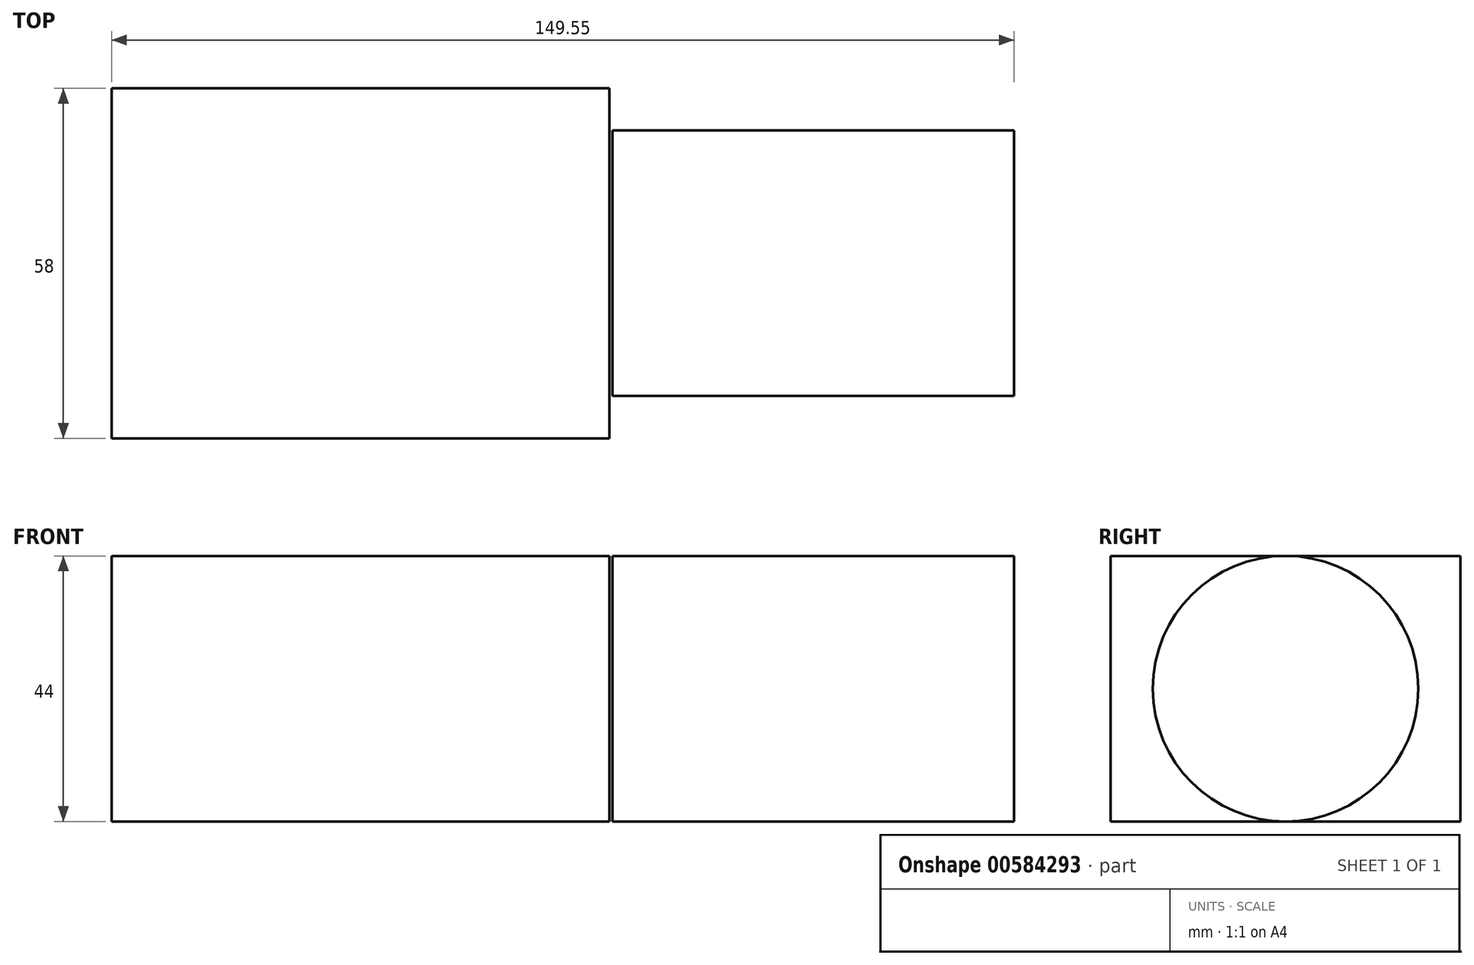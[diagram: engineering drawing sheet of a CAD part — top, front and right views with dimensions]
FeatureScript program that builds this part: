
annotation { "Feature Type Name" : "Feature", "Feature Type Description" : "" }
export const myFeature = defineFeature(function(context is Context, id is Id, definition is map)
    precondition{}
    {
        {
            var Q0;
            Q0=qCreatedBy(makeId("Front.planeOp"),FACE);
            var sketch = newSketch(context, id + "F0", { "sketchPlane" : qUnion([Q0])});
            skLineSegment(sketch, "E0.bottom", {"start": v(41.25, 22) * mm, "end": v(-41.25, 22) * mm});
            skLineSegment(sketch, "E0.top", {"start": v(41.25, -22) * mm, "end": v(-41.25, -22) * mm});
            skLineSegment(sketch, "E0.left", {"start": v(41.25, 22) * mm, "end": v(41.25, -22) * mm});
            skLineSegment(sketch, "E0.right", {"start": v(-41.25, 22) * mm, "end": v(-41.25, -22) * mm});
            skPoint(sketch, "E0.middle", {"position": v(0, 0) * mm});
            skLineSegment(sketch, "E1", {"start": v(41.25, 0) * mm, "end": v(107.78, 0) * mm});
            skPoint(sketch, "E1.endSnap0", {"position": v(41.25, 0) * mm});
            skSolve(sketch);
        }
        {
            var Q0;
            Q0=qCreatedBy(makeId("Front.planeOp"),FACE);
            var sketch = newSketch(context, id + "F1", { "sketchPlane" : qUnion([Q0])});
            skLineSegment(sketch, "E2.bottom", {"start": v(41.77, 0) * mm, "end": v(108.3, 0) * mm});
            skLineSegment(sketch, "E2.top", {"start": v(41.77, 22) * mm, "end": v(108.3, 22) * mm});
            skLineSegment(sketch, "E2.left", {"start": v(41.77, 0) * mm, "end": v(41.77, 22) * mm});
            skLineSegment(sketch, "E2.right", {"start": v(108.3, 0) * mm, "end": v(108.3, 22) * mm});
            skSolve(sketch);
        }
        {
            var Q0;
            Q0=makeQuery(id+"F1.imprint","IMPRINT",FACE,{"disambiguationData":[TD([[makeQuery(id+"F1.imprint","IMPRINT",EDGE,{"derivedFrom":sQuery(id+"F1.wireOp",EDGE,"E2.bottom")}),1.0]])]});
            var Q1;
            Q1=sQuery(id+"F1.wireOp",EDGE,"E2.bottom");
            revolve(context, id + "F2", {"entities" : qUnion([Q0]), "axis" : qUnion([Q1]), "revolveType" : RevolveType.FULL});
        }
        {
            var Q0;
            {var subQ3=sQuery(id+"F0.wireOp",EDGE,"E0.bottom");Q0=makeQuery(id+"F0.imprint","IMPRINT",FACE,{"disambiguationData":[TD([[makeQuery(id+"F0.imprint","IMPRINT",EDGE,{"derivedFrom":subQ3}),1.0]])]});}
            extrude(context, id + "F3", {"entities" : qUnion([Q0]), "endBound" : BoundingType.SYMMETRIC, "depth" : 58 * mm, "offsetDistance" : 25.4 * mm});
        }
    });
